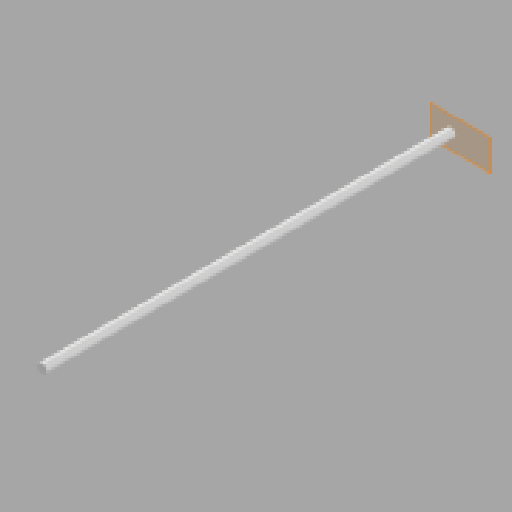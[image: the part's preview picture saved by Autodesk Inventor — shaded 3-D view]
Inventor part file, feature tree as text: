
AUTODESK INVENTOR PART (.ipt)
format: ipt  version: 2025 (Build 290162000, 162)  size: 82,432 bytes
history: native  units: in
note: dims shown in document units (in); Inventor stores cm internally (conversion verified against a paired STEP export)
features: other x2, plane x1, extrude x1, sketch x1, reference x1
ambient origin geometry x8: Origin, YZ Plane, XZ Plane, XY Plane, X Axis, Y Axis, Z Axis, Center Point
bodies: Solid1 (feature_tree)
feature tree (6):
  plane  "Work Plane1"
  extrude  "Extrusion1"  Depth=0.5in
  sketch  "Sketch1"  dims[d0=1.0in d1=9.0in d2=44.0in d3=0.0in d4=0.5in d5=0.0344in d6=0.5in d7=0.0344in]
  reference  "Reference1"
  other  "UAV_Assembly_1.0.iam"
  other  "WingBox:1"
